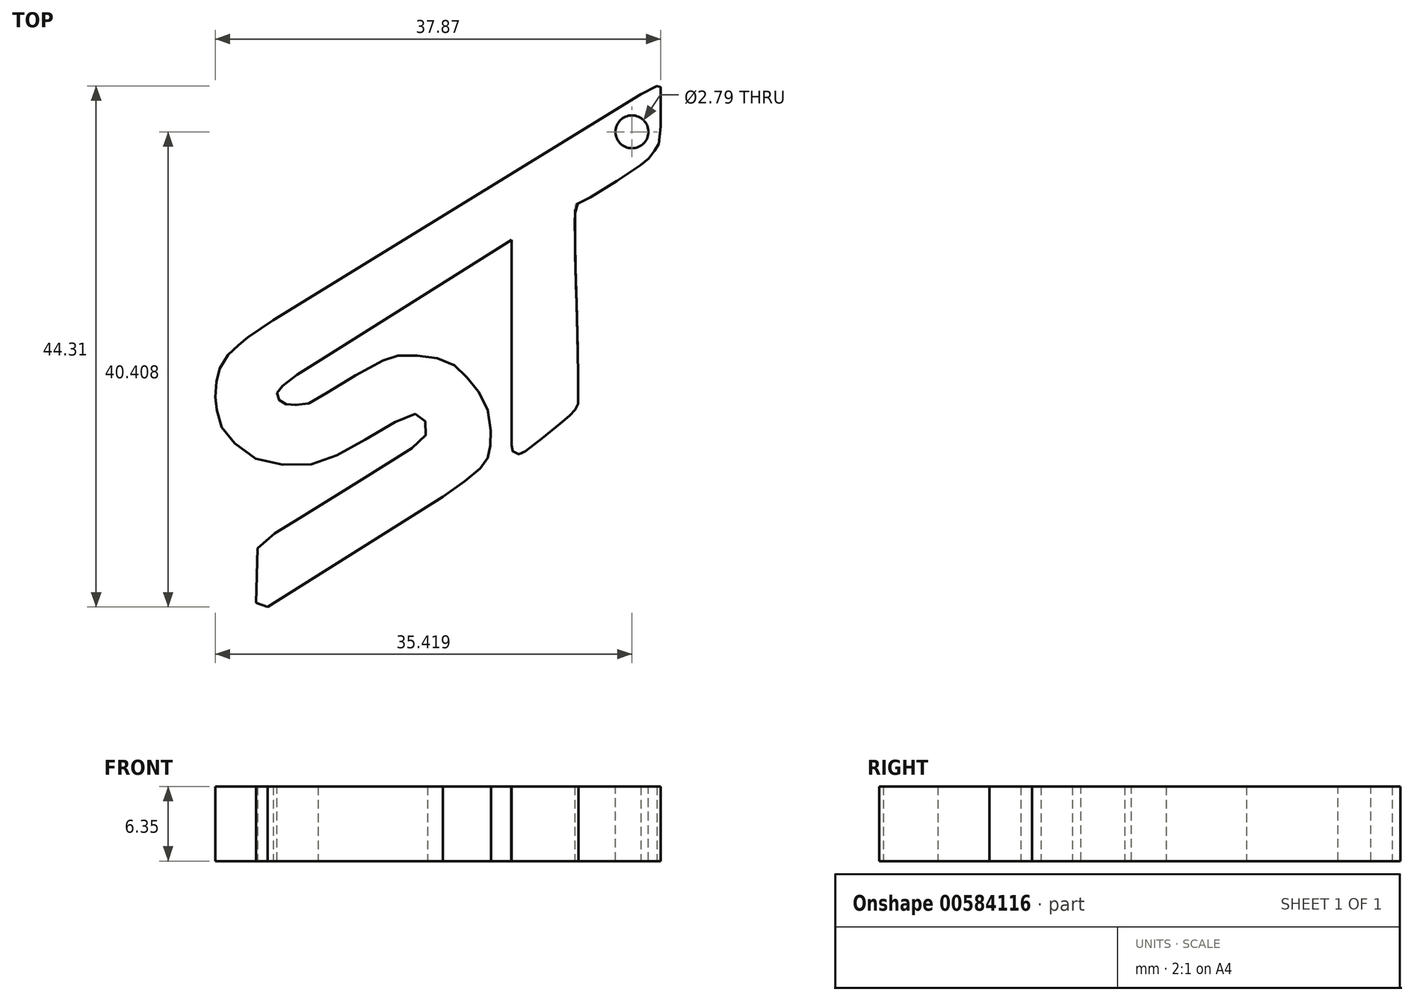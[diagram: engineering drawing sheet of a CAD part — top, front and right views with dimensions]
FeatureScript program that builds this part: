
annotation { "Feature Type Name" : "Feature", "Feature Type Description" : "" }
export const myFeature = defineFeature(function(context is Context, id is Id, definition is map)
    precondition{}
    {
        {
            var Q0;
            Q0=qCreatedBy(makeId("Top.planeOp"),FACE);
            var sketch = newSketch(context, id + "F0", { "sketchPlane" : qUnion([Q0])});
            skLineSegment(sketch, "E0", {"start": v(30.93, -38.54) * mm, "end": v(60.28, -49.33) * mm});
            skLineSegment(sketch, "E1", {"start": v(60.28, -49.33) * mm, "end": v(74.4, -49.33) * mm});
            skLineSegment(sketch, "E2", {"start": v(74.4, -49.33) * mm, "end": v(74.4, 2.82) * mm});
            skLineSegment(sketch, "E3", {"start": v(74.4, 2.82) * mm, "end": v(35.28, 2.82) * mm});
            skFitSpline(sketch, "E4", {"points": [v(35.28, 2.82) * mm, v(35.28, 1.02) * mm, v(35.46, -1.94) * mm, v(35.55, -3.3) * mm, v(35.6, -4.41) * mm, v(35.28, -5.2) * mm, v(34.82, -5.87) * mm, v(34.05, -6.36) * mm, v(33.08, -6.65) * mm, v(32.01, -6.65) * mm, v(31.14, -6.65) * mm], "startDerivative": vector(-0.3, -13.38) * mm, "endDerivative": vector(-10, -0.19) * mm});
            skFitSpline(sketch, "E5", {"points": [v(31.14, -6.65) * mm, v(31.14, -9.46) * mm, v(31.14, -10.2) * mm, v(31.42, -10.7) * mm, v(31.62, -11.28) * mm, v(31.6, -13.19) * mm, v(31.69, -15.26) * mm, v(32.08, -16.67) * mm, v(34.31, -19.53) * mm, v(34.9, -20.4) * mm, v(35.28, -21.15) * mm, v(35.43, -21.93) * mm, v(35.28, -22.88) * mm, v(34.77, -23.6) * mm, v(33.6, -24.83) * mm, v(32.76, -25.96) * mm, v(32.28, -27.46) * mm, v(32.04, -28.53) * mm, v(31.94, -29.8) * mm, v(31.26, -30.38) * mm, v(30.93, -30.57) * mm, v(30.85, -30.96) * mm, v(30.93, -31.4) * mm, v(31.27, -32.28) * mm, v(31.98, -33.37) * mm, v(32.36, -33.9) * mm, v(32.56, -34.49) * mm, v(32.74, -35.22) * mm, v(32.69, -35.9) * mm, v(30.93, -38.54) * mm], "startDerivative": vector(1.16, -59.6) * mm, "endDerivative": vector(-39.66, -52.77) * mm});
            skLineSegment(sketch, "E6", {"start": v(40.36, -42) * mm, "end": v(55.24, -32.64) * mm});
            skLineSegment(sketch, "E7", {"start": v(39.37, -41.64) * mm, "end": v(39.48, -37.02) * mm});
            skLineSegment(sketch, "E8", {"start": v(72.06, 1.6) * mm, "end": v(40.83, -17.62) * mm});
            skLineSegment(sketch, "E9", {"start": v(44.65, -21.13) * mm, "end": v(60.71, -11.03) * mm});
            skLineSegment(sketch, "E10", {"start": v(60.71, -11.03) * mm, "end": v(61.07, -10.8) * mm});
            skLineSegment(sketch, "E11", {"start": v(61.07, -10.8) * mm, "end": v(61.07, -28.26) * mm});
            skLineSegment(sketch, "E12", {"start": v(61.07, -28.26) * mm, "end": v(60.95, -28.26) * mm});
            skFitSpline(sketch, "E13", {"points": [v(40.83, -17.62) * mm, v(38.52, -19.19) * mm, v(38.23, -19.43) * mm, v(37.89, -19.72) * mm, v(37.45, -20.1) * mm, v(36.92, -20.64) * mm, v(36.48, -21.32) * mm, v(36.19, -21.95) * mm, v(36.04, -22.48) * mm, v(35.95, -23.16) * mm, v(35.9, -24.04) * mm, v(35.9, -24.52) * mm, v(36, -25.06) * mm, v(36.22, -25.98) * mm, v(36.6, -27.01) * mm, v(37.58, -28.11) * mm, v(39.33, -29.4) * mm, v(41.66, -29.9) * mm, v(44.3, -29.84) * mm, v(46.57, -28.92) * mm, v(49.74, -27.13) * mm, v(52.3, -25.7) * mm, v(53.03, -25.61) * mm, v(53.46, -25.9) * mm, v(53.8, -26.34) * mm, v(53.95, -26.82) * mm, v(53.66, -27.65) * mm, v(52.93, -28.28) * mm, v(42.27, -34.92) * mm, v(40.83, -35.85) * mm, v(39.48, -37.02) * mm], "startDerivative": vector(-59.7, -39.55) * mm, "endDerivative": vector(-38.06, -34.2) * mm});
            skFitSpline(sketch, "E14", {"points": [v(44.65, -21.13) * mm, v(42.53, -22.48) * mm, v(41.56, -23.23) * mm, v(41.28, -23.48) * mm, v(41.15, -23.8) * mm, v(41.15, -24.05) * mm, v(41.24, -24.3) * mm, v(41.37, -24.46) * mm, v(41.6, -24.65) * mm, v(41.81, -24.74) * mm, v(42.22, -24.8) * mm, v(42.6, -24.84) * mm, v(43.16, -24.8) * mm, v(43.98, -24.65) * mm, v(45.9, -23.45) * mm, v(50, -21.13) * mm, v(51.1, -20.7) * mm, v(52.42, -20.58) * mm, v(54.1, -20.76) * mm, v(55.65, -21.13) * mm, v(56.78, -21.93) * mm, v(57.54, -22.78) * mm, v(58.5, -24.06) * mm, v(59.18, -25.7) * mm, v(59.32, -27.4) * mm, v(59.28, -28.26) * mm, v(59.13, -29) * mm, v(58.99, -29.5) * mm, v(58.6, -30.03) * mm, v(57.58, -30.95) * mm, v(55.24, -32.64) * mm], "startDerivative": vector(-43.42, -26.35) * mm, "endDerivative": vector(-45.4, -31.66) * mm});
            skFitSpline(sketch, "E15", {"points": [v(61.07, -28.26) * mm, v(61.07, -28.55) * mm, v(61.24, -28.83) * mm, v(61.52, -28.99) * mm, v(61.87, -28.99) * mm, v(62.34, -28.7) * mm, v(65.3, -26.35) * mm, v(66.05, -25.7) * mm, v(66.4, -25.37) * mm, v(66.62, -25.03) * mm, v(66.74, -24.55) * mm, v(66.51, -7.96) * mm, v(66.63, -7.75) * mm, v(67.23, -7.48) * mm, v(72.2, -4.32) * mm, v(72.72, -3.87) * mm, v(73.1, -3.42) * mm, v(73.47, -2.83) * mm, v(73.7, -2.23) * mm, v(73.74, 2.03) * mm, v(73.75, 2.16) * mm, v(73.7, 2.27) * mm, v(73.6, 2.3) * mm, v(73.44, 2.28) * mm, v(73.25, 2.18) * mm, v(72.16, 1.6) * mm], "startDerivative": vector(-1.52, -13.02) * mm, "endDerivative": vector(-28.45, -14.92) * mm});
            skFitSpline(sketch, "E16", {"points": [v(72.06, 1.6) * mm, v(73.44, 2.28) * mm], "startDerivative": vector(1.39, 0.7) * mm, "endDerivative": vector(1.39, 0.7) * mm});
            skSolve(sketch);
        }
        {
            var Q0;
            {var subQ4=sQuery(id+"F0.wireOp",EDGE,"E6");Q0=makeQuery(id+"F0.imprint","IMPRINT",FACE,{"disambiguationData":[TD([[makeQuery(id+"F0.imprint","IMPRINT",EDGE,{"derivedFrom":subQ4}),1.0]])]});}
            extrude(context, id + "F1", {"entities" : qUnion([Q0]), "depth" : 6.35 * mm, "offsetDistance" : 25.4 * mm});
        }
        {
            var Q0;
            Q0=makeQuery(id+"F1.opExtrude","CAP_FACE",FACE,{"disambiguationData":[OSD([sQuery(id+"F0.wireOp",EDGE,"E0"),sQuery(id+"F0.wireOp",EDGE,"E6"),sQuery(id+"F0.wireOp",EDGE,"E7"),sQuery(id+"F0.wireOp",EDGE,"E8"),sQuery(id+"F0.wireOp",EDGE,"E9"),sQuery(id+"F0.wireOp",EDGE,"E10"),sQuery(id+"F0.wireOp",EDGE,"E11"),sQuery(id+"F0.wireOp",EDGE,"E13"),sQuery(id+"F0.wireOp",EDGE,"E14"),sQuery(id+"F0.wireOp",EDGE,"E15"),sQuery(id+"F0.wireOp",EDGE,"E16")])],"isStart":false});
            var sketch = newSketch(context, id + "F2", { "sketchPlane" : qUnion([Q0])});
            skCircle(sketch, "E17", {"center": v(71.3, -1.6) * mm, "radius": 1.3 * mm});
            skSolve(sketch);
        }
        {
            var Q0;
            Q0=sQuery(id+"F2.wireOp",VERTEX,"E17.center");
            var Q1;
            Q1=makeQuery(id+"F1.opExtrude","SWEPT_BODY",BODY,{"disambiguationData":[OSD([sQuery(id+"F0.wireOp",EDGE,"E0"),sQuery(id+"F0.wireOp",EDGE,"E6"),sQuery(id+"F0.wireOp",EDGE,"E7"),sQuery(id+"F0.wireOp",EDGE,"E8"),sQuery(id+"F0.wireOp",EDGE,"E9"),sQuery(id+"F0.wireOp",EDGE,"E10"),sQuery(id+"F0.wireOp",EDGE,"E11"),sQuery(id+"F0.wireOp",EDGE,"E13"),sQuery(id+"F0.wireOp",EDGE,"E14"),sQuery(id+"F0.wireOp",EDGE,"E15"),sQuery(id+"F0.wireOp",EDGE,"E16")])]});
            hole(context, id + "F3", {"style" : HoleStyle.SIMPLE, "endStyle" : HoleEndStyle.THROUGH, "holeDiameter" : 2.8 * mm, "majorDiameter" : 6.35 * mm, "isTappedThrough" : true, "tappedDepth" : 12.7 * mm, "tapClearance" : 3, "locations" : qUnion([Q0]), "scope" : qUnion([Q1])});
        }
    });
